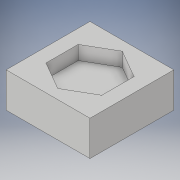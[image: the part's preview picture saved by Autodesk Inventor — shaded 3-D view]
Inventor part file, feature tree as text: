
AUTODESK INVENTOR PART (.ipt)
format: ipt  version: 2019 (Build 230136000, 136)  size: 102,400 bytes
history: native  units: in
note: dims shown in document units (in); Inventor stores cm internally (conversion verified against a paired STEP export)
features: extrude x2, sketch x2
ambient origin geometry x8: Origin, YZ Plane, XZ Plane, XY Plane, X Axis, Y Axis, Z Axis, Center Point
bodies: Solid1 (feature_tree)
feature tree (4):
  extrude  "Extrusion1"  Depth=0.4724in
  extrude  "Extrusion2"  Depth=0.0787in TaperAngle=0.0deg
  sketch  "Sketch1"  dims[d0=0.4724in d1=0.4724in]
  sketch  "Sketch2"  dims[d2=0.1969in d3=0.0in d6=0.0787in d7=0.0in d8=0.315in]
